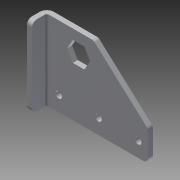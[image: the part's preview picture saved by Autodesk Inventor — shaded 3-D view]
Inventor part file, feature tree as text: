
AUTODESK INVENTOR PART (.ipt)
format: ipt  version: 2014 (Build 180170000, 170)  size: 131,584 bytes
history: native  units: in
note: dims shown in document units (in); Inventor stores cm internally (conversion verified against a paired STEP export)
features: sheet_metal_op x4, sketch x2, other x2, fillet x1
ambient origin geometry x8: Origin, YZ Plane, XZ Plane, XY Plane, X Axis, Y Axis, Z Axis, Center Point
bodies: Solid1 (feature_tree)
feature tree (9):
  sheet_metal_op  "Face1"
  sheet_metal_op  "Flange2"
  fillet  "Fillet1"  Radius=0.125in
  sketch  "Sketch1"  dims[d5=2.5in d6=0.163in d7=0.25in d8=0.375in d11=0.125in]
  other  "Plate1"
  sketch  "Sketch3"  dims[d22=1.1811in d24=1.0in d25=0.3937in d27=1.0in d29=2.0in d30=0.75in d31=1.125in d32=0.5in d34=0.75in d35=0.5in d36=0.125in d37=0.0625in d38=0.25in d39=0.125in d40=0.5in d41=90.0deg d42=0.05in d43=0.5in d44=0.125in d45=0.125in d46=0.125in]
  other  "Plate3"
  sheet_metal_op  "Bend2"
  sheet_metal_op  "Corner2"
